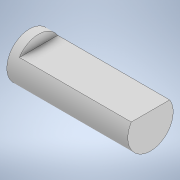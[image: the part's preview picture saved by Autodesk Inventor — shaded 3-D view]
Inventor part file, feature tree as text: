
AUTODESK INVENTOR PART (.ipt)
format: ipt  version: 2022 (Build 260153000, 153)  size: 103,936 bytes
history: native  units: mm
features: extrude x2, sketch x2
ambient origin geometry x8: Origin, YZ Plane, XZ Plane, XY Plane, X Axis, Y Axis, Z Axis, Center Point
bodies: 实体1 (feature_tree)
feature tree (4):
  extrude  "拉伸1"  Depth=0.6mm TaperAngle=0.0deg
  extrude  "拉伸2"  Depth=7.4mm TaperAngle=0.0deg
  sketch  "草图1"  dims[d0=3.0mm d1=0.6mm d2=0.0mm]
  sketch  "草图2"  dims[d3=2.3mm d4=7.4mm d5=0.0mm]
